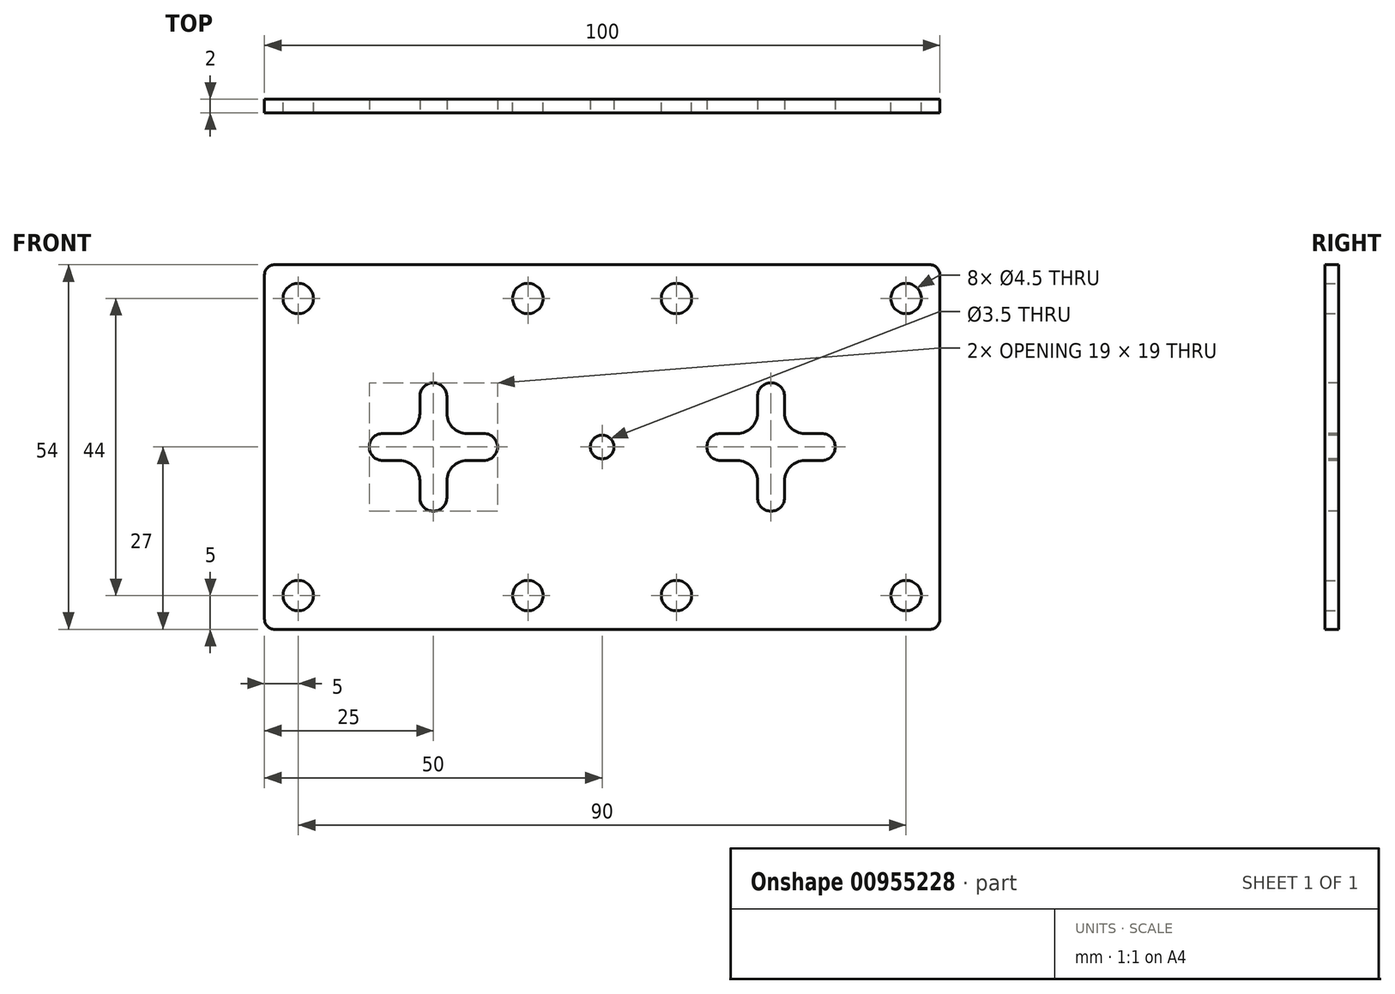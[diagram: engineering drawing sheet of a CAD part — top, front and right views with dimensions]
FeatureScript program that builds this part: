
annotation { "Feature Type Name" : "Feature", "Feature Type Description" : "" }
export const myFeature = defineFeature(function(context is Context, id is Id, definition is map)
    precondition{}
    {
        {
            var Q0;
            Q0=qCreatedBy(makeId("Front.planeOp"),FACE);
            var sketch = newSketch(context, id + "F0", { "sketchPlane" : qUnion([Q0])});
            skLineSegment(sketch, "E0.bottom", {"start": v(0, 0) * mm, "end": v(100, 0) * mm});
            skLineSegment(sketch, "E0.top", {"start": v(0, 54) * mm, "end": v(100, 54) * mm});
            skLineSegment(sketch, "E0.left", {"start": v(0, 0) * mm, "end": v(0, 54) * mm});
            skCircle(sketch, "E1", {"center": v(5, 49) * mm, "radius": 2.25 * mm});
            skCircle(sketch, "E2", {"center": v(39, 49) * mm, "radius": 2.25 * mm});
            skCircle(sketch, "E3", {"center": v(5, 5) * mm, "radius": 2.25 * mm});
            skCircle(sketch, "E4", {"center": v(39, 5) * mm, "radius": 2.25 * mm});
            skLineSegment(sketch, "E5.1.0.0", {"start": v(100, 0) * mm, "end": v(100, 54) * mm});
            skCircle(sketch, "E5.1.0.1", {"center": v(95, 49) * mm, "radius": 2.25 * mm});
            skCircle(sketch, "E5.1.0.2", {"center": v(61, 49) * mm, "radius": 2.25 * mm});
            skCircle(sketch, "E5.1.0.3", {"center": v(61, 5) * mm, "radius": 2.25 * mm});
            skCircle(sketch, "E5.1.0.4", {"center": v(95, 5) * mm, "radius": 2.25 * mm});
            skPoint(sketch, "E6.orphan", {"position": v(100, 11.45) * mm});
            skSolve(sketch);
        }
        {
            var Q0;
            Q0=makeQuery(id+"F0.imprint","IMPRINT",FACE,{"disambiguationData":[TD([[makeQuery(id+"F0.imprint","IMPRINT",EDGE,{"derivedFrom":sQuery(id+"F0.wireOp",EDGE,"E4")}),-1.0]])]});
            var Q1;
            {var subQ0=sQuery(id+"F0.wireOp",EDGE,"GIEVjX8B-AwTq-21Lb-ZbtB-CkMobrvajzeg");var subQ1=sQuery(id+"F0.wireOp",EDGE,"E3");var subQ9=makeQuery(id+"F0.imprint","INTERSECT",VERTEX,{"disambiguationData":[OD(0.0)],"derivedFrom":[subQ1,subQ0]});Q1=makeQuery(id+"F0.imprint","IMPRINT",FACE,{"disambiguationData":[TD([[makeQuery(id+"F0.imprint","IMPRINT",EDGE,{"disambiguationData":[TD([[subQ9,-1.0]])],"derivedFrom":subQ1}),-1.0]])]});}
            var Q2;
            {var subQ0=sQuery(id+"F0.wireOp",EDGE,"GIEVjX8B-AwTq-21Lb-ZbtB-CkMobrvajzeg");var subQ3=sQuery(id+"F0.wireOp",EDGE,"E3");var subQ4=makeQuery(id+"F0.imprint","INTERSECT",VERTEX,{"disambiguationData":[OD(0.0)],"derivedFrom":[subQ3,subQ0]});Q2=makeQuery(id+"F0.imprint","IMPRINT",FACE,{"disambiguationData":[TD([[makeQuery(id+"F0.imprint","IMPRINT",EDGE,{"disambiguationData":[TD([[subQ4,1.0]])],"derivedFrom":subQ3}),-1.0]])]});}
            var Q3;
            Q3=makeQuery(id+"F0.imprint","IMPRINT",FACE,{"disambiguationData":[TD([[makeQuery(id+"F0.imprint","IMPRINT",EDGE,{"derivedFrom":sQuery(id+"F0.wireOp",EDGE,"E1")}),-1.0]])]});
            var Q4;
            {var subQ0=sQuery(id+"F0.wireOp",EDGE,"GIEVjX8B-AwTq-21Lb-ZbtB-CkMobrvajzeg");var subQ1=sQuery(id+"F0.wireOp",EDGE,"E2");var subQ2=makeQuery(id+"F0.imprint","INTERSECT",VERTEX,{"disambiguationData":[OD(0.0)],"derivedFrom":[subQ1,subQ0]});Q4=makeQuery(id+"F0.imprint","IMPRINT",FACE,{"disambiguationData":[TD([[makeQuery(id+"F0.imprint","IMPRINT",EDGE,{"disambiguationData":[TD([[subQ2,1.0]])],"derivedFrom":subQ1}),-1.0]])]});}
            var Q5;
            {var subQ0=sQuery(id+"F0.wireOp",EDGE,"7TBIhXpD-YLFU-Nl18-vzzi-2WDcdoC6Z20b");Q5=makeQuery(id+"F0.imprint","IMPRINT",FACE,{"disambiguationData":[TD([[makeQuery(id+"F0.imprint","IMPRINT",EDGE,{"derivedFrom":subQ0}),1.0]])]});}
            var Q6;
            Q6=makeQuery(id+"F0.imprint","IMPRINT",FACE,{"disambiguationData":[TD([[makeQuery(id+"F0.imprint","IMPRINT",EDGE,{"derivedFrom":sQuery(id+"F0.wireOp",EDGE,"y2sm0lNR-VdRE-JFiU-62jz-dkLi8y3kCuxd")}),-1.0]])]});
            var Q7;
            {var subQ0=sQuery(id+"F0.wireOp",EDGE,"OQeiLcVa-iH9X-DJD4-n5DP-qmeMiz6CTvk2");var subQ1=sQuery(id+"F0.wireOp",EDGE,"zRPmDN4C-YppU-B8H8-Iecn-RaXdhoolfD6k");var subQ2=makeQuery(id+"F0.imprint","INTERSECT",VERTEX,{"disambiguationData":[OD(1.0)],"derivedFrom":[subQ1,subQ0]});Q7=makeQuery(id+"F0.imprint","IMPRINT",FACE,{"disambiguationData":[TD([[makeQuery(id+"F0.imprint","IMPRINT",EDGE,{"disambiguationData":[TD([[subQ2,1.0]])],"derivedFrom":subQ1}),1.0]])]});}
            var Q8;
            {var subQ0=sQuery(id+"F0.wireOp",EDGE,"OQeiLcVa-iH9X-DJD4-n5DP-qmeMiz6CTvk2");var subQ1=sQuery(id+"F0.wireOp",EDGE,"GIEVjX8B-AwTq-21Lb-ZbtB-CkMobrvajzeg");var subQ2=makeQuery(id+"F0.imprint","INTERSECT",VERTEX,{"disambiguationData":[OD(0.0)],"derivedFrom":[subQ1,subQ0]});Q8=makeQuery(id+"F0.imprint","IMPRINT",FACE,{"disambiguationData":[TD([[makeQuery(id+"F0.imprint","IMPRINT",EDGE,{"disambiguationData":[TD([[subQ2,-1.0]])],"derivedFrom":subQ1}),-1.0]])]});}
            var Q9;
            {var subQ0=sQuery(id+"F0.wireOp",EDGE,"OQeiLcVa-iH9X-DJD4-n5DP-qmeMiz6CTvk2");var subQ1=sQuery(id+"F0.wireOp",EDGE,"GIEVjX8B-AwTq-21Lb-ZbtB-CkMobrvajzeg");var subQ2=makeQuery(id+"F0.imprint","INTERSECT",VERTEX,{"disambiguationData":[OD(0.0)],"derivedFrom":[subQ1,subQ0]});Q9=makeQuery(id+"F0.imprint","IMPRINT",FACE,{"disambiguationData":[TD([[makeQuery(id+"F0.imprint","IMPRINT",EDGE,{"disambiguationData":[TD([[subQ2,-1.0]])],"derivedFrom":subQ1}),1.0]])]});}
            var Q10;
            {var subQ0=sQuery(id+"F0.wireOp",EDGE,"OQeiLcVa-iH9X-DJD4-n5DP-qmeMiz6CTvk2");var subQ1=sQuery(id+"F0.wireOp",EDGE,"zRPmDN4C-YppU-B8H8-Iecn-RaXdhoolfD6k");var subQ2=makeQuery(id+"F0.imprint","INTERSECT",VERTEX,{"disambiguationData":[OD(0.0)],"derivedFrom":[subQ1,subQ0]});Q10=makeQuery(id+"F0.imprint","IMPRINT",FACE,{"disambiguationData":[TD([[makeQuery(id+"F0.imprint","IMPRINT",EDGE,{"disambiguationData":[TD([[subQ2,-1.0]])],"derivedFrom":subQ1}),-1.0]])]});}
            var Q11;
            {var subQ0=sQuery(id+"F0.wireOp",EDGE,"J005bBo2-tTAp-IIAb-LBN8-FGsRf0HitLGd");var subQ1=sQuery(id+"F0.wireOp",EDGE,"GIEVjX8B-AwTq-21Lb-ZbtB-CkMobrvajzeg");var subQ2=makeQuery(id+"F0.imprint","INTERSECT",VERTEX,{"disambiguationData":[OD(1.0)],"derivedFrom":[subQ1,subQ0]});Q11=makeQuery(id+"F0.imprint","IMPRINT",FACE,{"disambiguationData":[TD([[makeQuery(id+"F0.imprint","IMPRINT",EDGE,{"disambiguationData":[TD([[subQ2,-1.0]])],"derivedFrom":subQ1}),1.0]])]});}
            var Q12;
            {var subQ0=sQuery(id+"F0.wireOp",EDGE,"J005bBo2-tTAp-IIAb-LBN8-FGsRf0HitLGd");var subQ1=sQuery(id+"F0.wireOp",EDGE,"GIEVjX8B-AwTq-21Lb-ZbtB-CkMobrvajzeg");var subQ2=makeQuery(id+"F0.imprint","INTERSECT",VERTEX,{"disambiguationData":[OD(1.0)],"derivedFrom":[subQ1,subQ0]});Q12=makeQuery(id+"F0.imprint","IMPRINT",FACE,{"disambiguationData":[TD([[makeQuery(id+"F0.imprint","IMPRINT",EDGE,{"disambiguationData":[TD([[subQ2,-1.0]])],"derivedFrom":subQ1}),-1.0]])]});}
            var Q13;
            {var subQ0=sQuery(id+"F0.wireOp",EDGE,"mIcQAeoJ-TY8I-UeRR-g85p-Uk80boknLbHP");var subQ1=sQuery(id+"F0.wireOp",EDGE,"GIEVjX8B-AwTq-21Lb-ZbtB-CkMobrvajzeg");var subQ2=makeQuery(id+"F0.imprint","INTERSECT",VERTEX,{"disambiguationData":[OD(1.0)],"derivedFrom":[subQ1,subQ0]});Q13=makeQuery(id+"F0.imprint","IMPRINT",FACE,{"disambiguationData":[TD([[makeQuery(id+"F0.imprint","IMPRINT",EDGE,{"disambiguationData":[TD([[subQ2,-1.0]])],"derivedFrom":subQ1}),-1.0]])]});}
            var Q14;
            {var subQ0=sQuery(id+"F0.wireOp",EDGE,"2wxwci7u-jRv2-8zPh-VqsC-HDhPEag0gPFr");var subQ1=sQuery(id+"F0.wireOp",EDGE,"GIEVjX8B-AwTq-21Lb-ZbtB-CkMobrvajzeg");var subQ2=makeQuery(id+"F0.imprint","INTERSECT",VERTEX,{"disambiguationData":[OD(1.0)],"derivedFrom":[subQ1,subQ0]});Q14=makeQuery(id+"F0.imprint","IMPRINT",FACE,{"disambiguationData":[TD([[makeQuery(id+"F0.imprint","IMPRINT",EDGE,{"disambiguationData":[TD([[subQ2,-1.0]])],"derivedFrom":subQ1}),-1.0]])]});}
            var Q15;
            {var subQ0=sQuery(id+"F0.wireOp",EDGE,"2wxwci7u-jRv2-8zPh-VqsC-HDhPEag0gPFr");var subQ1=sQuery(id+"F0.wireOp",EDGE,"GIEVjX8B-AwTq-21Lb-ZbtB-CkMobrvajzeg");var subQ2=makeQuery(id+"F0.imprint","INTERSECT",VERTEX,{"disambiguationData":[OD(1.0)],"derivedFrom":[subQ1,subQ0]});Q15=makeQuery(id+"F0.imprint","IMPRINT",FACE,{"disambiguationData":[TD([[makeQuery(id+"F0.imprint","IMPRINT",EDGE,{"disambiguationData":[TD([[subQ2,-1.0]])],"derivedFrom":subQ1}),1.0]])]});}
            var Q16;
            {var subQ0=sQuery(id+"F0.wireOp",EDGE,"mIcQAeoJ-TY8I-UeRR-g85p-Uk80boknLbHP");var subQ1=sQuery(id+"F0.wireOp",EDGE,"GIEVjX8B-AwTq-21Lb-ZbtB-CkMobrvajzeg");var subQ2=makeQuery(id+"F0.imprint","INTERSECT",VERTEX,{"disambiguationData":[OD(1.0)],"derivedFrom":[subQ1,subQ0]});Q16=makeQuery(id+"F0.imprint","IMPRINT",FACE,{"disambiguationData":[TD([[makeQuery(id+"F0.imprint","IMPRINT",EDGE,{"disambiguationData":[TD([[subQ2,-1.0]])],"derivedFrom":subQ1}),1.0]])]});}
            var Q17;
            {var subQ0=sQuery(id+"F0.wireOp",EDGE,"M3oJXdJR-jTPD-ANoR-Roan-Mx8eRias5JtN");var subQ1=sQuery(id+"F0.wireOp",EDGE,"GIEVjX8B-AwTq-21Lb-ZbtB-CkMobrvajzeg");var subQ2=makeQuery(id+"F0.imprint","INTERSECT",VERTEX,{"disambiguationData":[OD(1.0)],"derivedFrom":[subQ1,subQ0]});Q17=makeQuery(id+"F0.imprint","IMPRINT",FACE,{"disambiguationData":[TD([[makeQuery(id+"F0.imprint","IMPRINT",EDGE,{"disambiguationData":[TD([[subQ2,-1.0]])],"derivedFrom":subQ1}),1.0]])]});}
            var Q18;
            {var subQ0=sQuery(id+"F0.wireOp",EDGE,"BPwgNexN-K37r-2dNv-RT6k-s0HhYUOfqwyI");var subQ1=sQuery(id+"F0.wireOp",EDGE,"wY2lboNd-KgJP-PN7j-VAr6-WGaW0PwUoEyy");var subQ2=makeQuery(id+"F0.imprint","INTERSECT",VERTEX,{"derivedFrom":[subQ1,subQ0]});Q18=makeQuery(id+"F0.imprint","IMPRINT",FACE,{"disambiguationData":[TD([[makeQuery(id+"F0.imprint","IMPRINT",EDGE,{"disambiguationData":[TD([[subQ2,-1.0]])],"derivedFrom":subQ1}),1.0]])]});}
            var Q19;
            {var subQ1=sQuery(id+"F0.wireOp",EDGE,"GIEVjX8B-AwTq-21Lb-ZbtB-CkMobrvajzeg");var subQ5=sQuery(id+"F0.wireOp",EDGE,"2wxwci7u-jRv2-8zPh-VqsC-HDhPEag0gPFr");var subQ6=makeQuery(id+"F0.imprint","INTERSECT",VERTEX,{"disambiguationData":[OD(0.0)],"derivedFrom":[subQ1,subQ5]});Q19=makeQuery(id+"F0.imprint","IMPRINT",FACE,{"disambiguationData":[TD([[makeQuery(id+"F0.imprint","IMPRINT",EDGE,{"disambiguationData":[TD([[subQ6,-1.0]])],"derivedFrom":subQ1}),1.0]])]});}
            var Q20;
            {var subQ0=sQuery(id+"F0.wireOp",EDGE,"2wxwci7u-jRv2-8zPh-VqsC-HDhPEag0gPFr");var subQ1=sQuery(id+"F0.wireOp",EDGE,"GIEVjX8B-AwTq-21Lb-ZbtB-CkMobrvajzeg");var subQ2=makeQuery(id+"F0.imprint","INTERSECT",VERTEX,{"disambiguationData":[OD(0.0)],"derivedFrom":[subQ1,subQ0]});Q20=makeQuery(id+"F0.imprint","IMPRINT",FACE,{"disambiguationData":[TD([[makeQuery(id+"F0.imprint","IMPRINT",EDGE,{"disambiguationData":[TD([[subQ2,-1.0]])],"derivedFrom":subQ1}),-1.0]])]});}
            var Q21;
            {var subQ0=sQuery(id+"F0.wireOp",EDGE,"M3oJXdJR-jTPD-ANoR-Roan-Mx8eRias5JtN");var subQ3=sQuery(id+"F0.wireOp",EDGE,"wY2lboNd-KgJP-PN7j-VAr6-WGaW0PwUoEyy");var subQ4=makeQuery(id+"F0.imprint","INTERSECT",VERTEX,{"disambiguationData":[OD(1.0)],"derivedFrom":[subQ3,subQ0]});Q21=makeQuery(id+"F0.imprint","IMPRINT",FACE,{"disambiguationData":[TD([[makeQuery(id+"F0.imprint","IMPRINT",EDGE,{"disambiguationData":[TD([[subQ4,-1.0]])],"derivedFrom":subQ3}),-1.0]])]});}
            var Q22;
            {var subQ5=sQuery(id+"F0.wireOp",EDGE,"M3oJXdJR-jTPD-ANoR-Roan-Mx8eRias5JtN");var subQ6=sQuery(id+"F0.wireOp",EDGE,"GIEVjX8B-AwTq-21Lb-ZbtB-CkMobrvajzeg");var subQ7=makeQuery(id+"F0.imprint","INTERSECT",VERTEX,{"disambiguationData":[OD(1.0)],"derivedFrom":[subQ6,subQ5]});Q22=makeQuery(id+"F0.imprint","IMPRINT",FACE,{"disambiguationData":[TD([[makeQuery(id+"F0.imprint","IMPRINT",EDGE,{"disambiguationData":[TD([[subQ7,-1.0]])],"derivedFrom":subQ6}),-1.0]])]});}
            var Q23;
            {var subQ0=sQuery(id+"F0.wireOp",EDGE,"mIcQAeoJ-TY8I-UeRR-g85p-Uk80boknLbHP");var subQ1=sQuery(id+"F0.wireOp",EDGE,"GIEVjX8B-AwTq-21Lb-ZbtB-CkMobrvajzeg");var subQ2=makeQuery(id+"F0.imprint","INTERSECT",VERTEX,{"disambiguationData":[OD(0.0)],"derivedFrom":[subQ1,subQ0]});Q23=makeQuery(id+"F0.imprint","IMPRINT",FACE,{"disambiguationData":[TD([[makeQuery(id+"F0.imprint","IMPRINT",EDGE,{"disambiguationData":[TD([[subQ2,-1.0]])],"derivedFrom":subQ1}),-1.0]])]});}
            var Q24;
            {var subQ0=sQuery(id+"F0.wireOp",EDGE,"J005bBo2-tTAp-IIAb-LBN8-FGsRf0HitLGd");var subQ1=sQuery(id+"F0.wireOp",EDGE,"GIEVjX8B-AwTq-21Lb-ZbtB-CkMobrvajzeg");var subQ2=makeQuery(id+"F0.imprint","INTERSECT",VERTEX,{"disambiguationData":[OD(0.0)],"derivedFrom":[subQ1,subQ0]});Q24=makeQuery(id+"F0.imprint","IMPRINT",FACE,{"disambiguationData":[TD([[makeQuery(id+"F0.imprint","IMPRINT",EDGE,{"disambiguationData":[TD([[subQ2,-1.0]])],"derivedFrom":subQ1}),-1.0]])]});}
            var Q25;
            {var subQ0=sQuery(id+"F0.wireOp",EDGE,"J005bBo2-tTAp-IIAb-LBN8-FGsRf0HitLGd");var subQ1=sQuery(id+"F0.wireOp",EDGE,"GIEVjX8B-AwTq-21Lb-ZbtB-CkMobrvajzeg");var subQ2=makeQuery(id+"F0.imprint","INTERSECT",VERTEX,{"disambiguationData":[OD(0.0)],"derivedFrom":[subQ1,subQ0]});Q25=makeQuery(id+"F0.imprint","IMPRINT",FACE,{"disambiguationData":[TD([[makeQuery(id+"F0.imprint","IMPRINT",EDGE,{"disambiguationData":[TD([[subQ2,-1.0]])],"derivedFrom":subQ1}),1.0]])]});}
            var Q26;
            {var subQ0=sQuery(id+"F0.wireOp",EDGE,"mIcQAeoJ-TY8I-UeRR-g85p-Uk80boknLbHP");var subQ1=sQuery(id+"F0.wireOp",EDGE,"GIEVjX8B-AwTq-21Lb-ZbtB-CkMobrvajzeg");var subQ2=makeQuery(id+"F0.imprint","INTERSECT",VERTEX,{"disambiguationData":[OD(0.0)],"derivedFrom":[subQ1,subQ0]});Q26=makeQuery(id+"F0.imprint","IMPRINT",FACE,{"disambiguationData":[TD([[makeQuery(id+"F0.imprint","IMPRINT",EDGE,{"disambiguationData":[TD([[subQ2,-1.0]])],"derivedFrom":subQ1}),1.0]])]});}
            var Q27;
            {var subQ6=sQuery(id+"F0.wireOp",EDGE,"E0.right");var subQ9=sQuery(id+"F0.wireOp",EDGE,"wY2lboNd-KgJP-PN7j-VAr6-WGaW0PwUoEyy");var subQ10=makeQuery(id+"F0.imprint","INTERSECT",VERTEX,{"derivedFrom":[subQ6,subQ9]});Q27=makeQuery(id+"F0.imprint","IMPRINT",FACE,{"disambiguationData":[TD([[makeQuery(id+"F0.imprint","IMPRINT",EDGE,{"disambiguationData":[TD([[subQ10,-1.0]])],"derivedFrom":subQ6}),1.0]])]});}
            extrude(context, id + "F1", {"entities" : qUnion([Q0, Q1, Q2, Q3, Q4, Q5, Q6, Q7, Q8, Q9, Q10, Q11, Q12, Q13, Q14, Q15, Q16, Q17, Q18, Q19, Q20, Q21, Q22, Q23, Q24, Q25, Q26, Q27]), "depth" : 2 * mm, "offsetDistance" : 25 * mm});
        }
        {
            var Q0;
            Q0=makeQuery(id+"F1.opExtrude","CAP_FACE",FACE,{"disambiguationData":[OSD([sQuery(id+"F0.wireOp",EDGE,"E0.bottom"),sQuery(id+"F0.wireOp",EDGE,"E0.top"),sQuery(id+"F0.wireOp",EDGE,"E0.left"),sQuery(id+"F0.wireOp",EDGE,"E1"),sQuery(id+"F0.wireOp",EDGE,"E2"),sQuery(id+"F0.wireOp",EDGE,"E3"),sQuery(id+"F0.wireOp",EDGE,"E4"),sQuery(id+"F0.wireOp",EDGE,"E5.1.0.0"),sQuery(id+"F0.wireOp",EDGE,"E5.1.0.1"),sQuery(id+"F0.wireOp",EDGE,"E5.1.0.2"),sQuery(id+"F0.wireOp",EDGE,"E5.1.0.3"),sQuery(id+"F0.wireOp",EDGE,"E5.1.0.4")])],"isStart":false});
            var sketch = newSketch(context, id + "F2", { "sketchPlane" : qUnion([Q0])});
            skLineSegment(sketch, "E7", {"start": v(17.5, 27) * mm, "end": v(32.5, 27) * mm});
            skLineSegment(sketch, "E8", {"start": v(25, 34.5) * mm, "end": v(25, 19.5) * mm});
            skArc(sketch, "E9.0.startCap", {"start": v(23, 34.5) * mm, "mid": v(25, 36.5) * mm, "end": v(27, 34.5) * mm});
            skArc(sketch, "E9.0.endCap", {"start": v(27, 19.5) * mm, "mid": v(25, 17.5) * mm, "end": v(23, 19.5) * mm});
            skLineSegment(sketch, "E9.0.left", {"start": v(27, 34.5) * mm, "end": v(27, 19.5) * mm});
            skLineSegment(sketch, "E9.0.right", {"start": v(23, 34.5) * mm, "end": v(23, 19.5) * mm});
            skArc(sketch, "E10.0.startCap", {"start": v(17.5, 25) * mm, "mid": v(15.5, 27) * mm, "end": v(17.5, 29) * mm});
            skArc(sketch, "E10.0.endCap", {"start": v(32.5, 29) * mm, "mid": v(34.5, 27) * mm, "end": v(32.5, 25) * mm});
            skLineSegment(sketch, "E10.0.left", {"start": v(17.5, 29) * mm, "end": v(32.5, 29) * mm});
            skLineSegment(sketch, "E10.0.right", {"start": v(17.5, 25) * mm, "end": v(32.5, 25) * mm});
            skCircle(sketch, "E11", {"center": v(50, 27) * mm, "radius": 1.75 * mm});
            skLineSegment(sketch, "E12.1.0.0", {"start": v(67.5, 27) * mm, "end": v(82.5, 27) * mm});
            skLineSegment(sketch, "E12.1.0.1", {"start": v(67.5, 29) * mm, "end": v(82.5, 29) * mm});
            skLineSegment(sketch, "E12.1.0.2", {"start": v(73, 34.5) * mm, "end": v(73, 19.5) * mm});
            skArc(sketch, "E12.1.0.3", {"start": v(77, 19.5) * mm, "mid": v(75, 17.5) * mm, "end": v(73, 19.5) * mm});
            skLineSegment(sketch, "E12.1.0.4", {"start": v(75, 34.5) * mm, "end": v(75, 19.5) * mm});
            skArc(sketch, "E12.1.0.5", {"start": v(67.5, 25) * mm, "mid": v(65.5, 27) * mm, "end": v(67.5, 29) * mm});
            skLineSegment(sketch, "E12.1.0.6", {"start": v(77, 34.5) * mm, "end": v(77, 19.5) * mm});
            skArc(sketch, "E12.1.0.7", {"start": v(73, 34.5) * mm, "mid": v(75, 36.5) * mm, "end": v(77, 34.5) * mm});
            skArc(sketch, "E12.1.0.8", {"start": v(82.5, 29) * mm, "mid": v(84.5, 27) * mm, "end": v(82.5, 25) * mm});
            skLineSegment(sketch, "E12.1.0.9", {"start": v(67.5, 25) * mm, "end": v(82.5, 25) * mm});
            skLineSegment(sketch, "E12.direction1", {"start": v(23, 19.5) * mm, "end": v(73, 19.5) * mm, "construction": true});
            skSolve(sketch);
        }
        {
            var Q0;
            Q0 = qSketchRegion(id + "F2", true);
            extrude(context, id + "F3", {"entities" : qUnion([Q0]), "operationType" : NewBodyOperationType.REMOVE, "oppositeDirection" : true, "depth" : 2 * mm, "offsetDistance" : 25 * mm});
        }
        {
            var Q0;
            Q0=makeQuery(id+"F3.boolean.opBoolean","COPY",EDGE,{"derivedFrom":makeQuery(id+"F3.opExtrude","SWEPT_EDGE",EDGE,{"disambiguationData":[OSD([sQuery(id+"F2.wireOp",EDGE,"E9.0.right"),sQuery(id+"F2.wireOp",EDGE,"E10.0.left")])]})});
            var Q1;
            Q1=makeQuery(id+"F3.boolean.opBoolean","COPY",EDGE,{"derivedFrom":makeQuery(id+"F3.opExtrude","SWEPT_EDGE",EDGE,{"disambiguationData":[OSD([sQuery(id+"F2.wireOp",EDGE,"E9.0.right"),sQuery(id+"F2.wireOp",EDGE,"E10.0.right")])]})});
            var Q2;
            Q2=makeQuery(id+"F3.boolean.opBoolean","COPY",EDGE,{"derivedFrom":makeQuery(id+"F3.opExtrude","SWEPT_EDGE",EDGE,{"disambiguationData":[OSD([sQuery(id+"F2.wireOp",EDGE,"E9.0.left"),sQuery(id+"F2.wireOp",EDGE,"E10.0.right")])]})});
            var Q3;
            Q3=makeQuery(id+"F3.boolean.opBoolean","COPY",EDGE,{"derivedFrom":makeQuery(id+"F3.opExtrude","SWEPT_EDGE",EDGE,{"disambiguationData":[OSD([sQuery(id+"F2.wireOp",EDGE,"E9.0.left"),sQuery(id+"F2.wireOp",EDGE,"E10.0.left")])]})});
            var Q4;
            Q4=makeQuery(id+"F3.boolean.opBoolean","COPY",EDGE,{"derivedFrom":makeQuery(id+"F3.opExtrude","SWEPT_EDGE",EDGE,{"disambiguationData":[OSD([sQuery(id+"F2.wireOp",EDGE,"E12.1.0.1"),sQuery(id+"F2.wireOp",EDGE,"E12.1.0.2")])]})});
            var Q5;
            Q5=makeQuery(id+"F3.boolean.opBoolean","COPY",EDGE,{"derivedFrom":makeQuery(id+"F3.opExtrude","SWEPT_EDGE",EDGE,{"disambiguationData":[OSD([sQuery(id+"F2.wireOp",EDGE,"E12.1.0.1"),sQuery(id+"F2.wireOp",EDGE,"E12.1.0.6")])]})});
            var Q6;
            Q6=makeQuery(id+"F3.boolean.opBoolean","COPY",EDGE,{"derivedFrom":makeQuery(id+"F3.opExtrude","SWEPT_EDGE",EDGE,{"disambiguationData":[OSD([sQuery(id+"F2.wireOp",EDGE,"E12.1.0.6"),sQuery(id+"F2.wireOp",EDGE,"E12.1.0.9")])]})});
            var Q7;
            Q7=makeQuery(id+"F3.boolean.opBoolean","COPY",EDGE,{"derivedFrom":makeQuery(id+"F3.opExtrude","SWEPT_EDGE",EDGE,{"disambiguationData":[OSD([sQuery(id+"F2.wireOp",EDGE,"E12.1.0.2"),sQuery(id+"F2.wireOp",EDGE,"E12.1.0.9")])]})});
            fillet(context, id + "F4", {"entities" : qUnion([Q0, Q1, Q2, Q3, Q4, Q5, Q6, Q7]), "radius" : 3 * mm, "tangentPropagation" : true, "allowEdgeOverflow" : false});
        }
        {
            var Q0;
            Q0=makeQuery(id+"F1.opExtrude","SWEPT_EDGE",EDGE,{"disambiguationData":[OSD([sQuery(id+"F0.wireOp",EDGE,"E0.top"),sQuery(id+"F0.wireOp",EDGE,"E0.right"),sQuery(id+"F0.wireOp",EDGE,"GIEVjX8B-AwTq-21Lb-ZbtB-CkMobrvajzeg")])]});
            var Q1;
            Q1=makeQuery(id+"F1.opExtrude","SWEPT_EDGE",EDGE,{"disambiguationData":[OSD([sQuery(id+"F0.wireOp",EDGE,"E0.top"),sQuery(id+"F0.wireOp",EDGE,"E0.left")])]});
            var Q2;
            Q2=makeQuery(id+"F1.opExtrude","SWEPT_EDGE",EDGE,{"disambiguationData":[OSD([sQuery(id+"F0.wireOp",EDGE,"E0.bottom"),sQuery(id+"F0.wireOp",EDGE,"E0.right")])]});
            var Q3;
            Q3=makeQuery(id+"F1.opExtrude","SWEPT_EDGE",EDGE,{"disambiguationData":[OSD([sQuery(id+"F0.wireOp",EDGE,"E0.bottom"),sQuery(id+"F0.wireOp",EDGE,"E0.left"),sQuery(id+"F0.wireOp",EDGE,"GIEVjX8B-AwTq-21Lb-ZbtB-CkMobrvajzeg")])]});
            fillet(context, id + "F5", {"entities" : qUnion([Q0, Q1, Q2, Q3]), "radius" : 1.5 * mm, "tangentPropagation" : true, "allowEdgeOverflow" : false});
        }
    });
